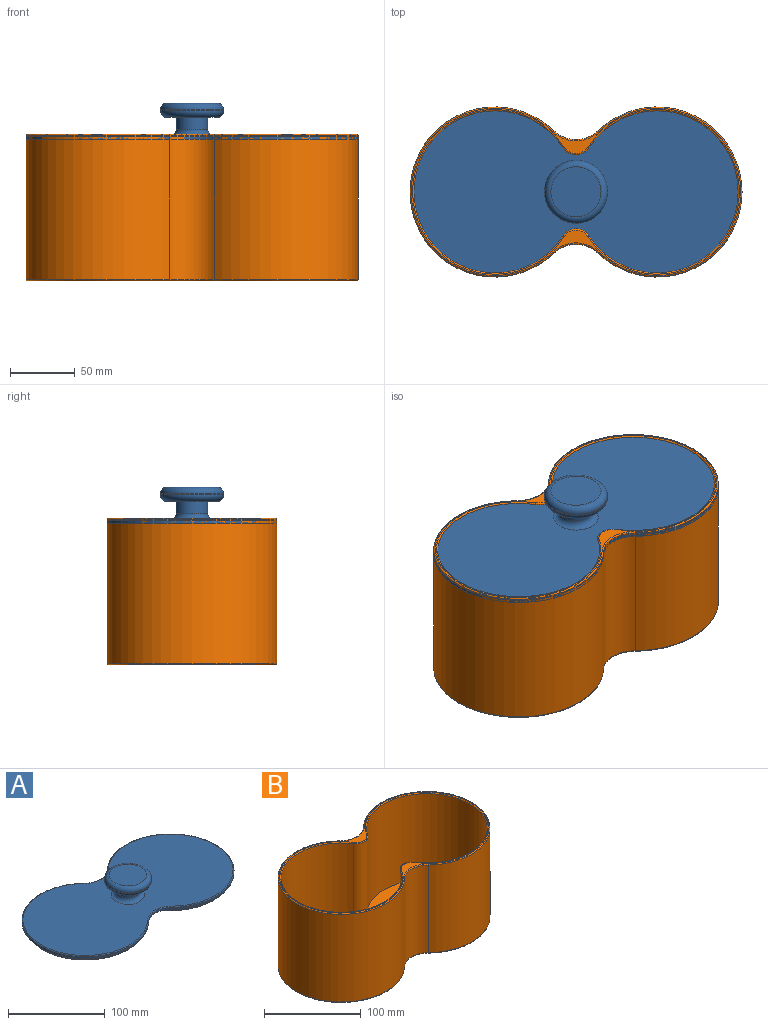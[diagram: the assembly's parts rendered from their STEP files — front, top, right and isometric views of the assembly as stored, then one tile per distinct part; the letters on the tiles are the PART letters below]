
ASSEMBLY  parts=2 mates=1
PART A: 26 faces, bbox 266.8x141.8x33 mm
  f0: cylinder r=24.76mm len=34.29mm, axis (0,0,-1), area 75.8mm2, adj f1,f3,f5,f22
  f1: cylinder r=65.5mm len=131mm, axis (0,0,-1), area 611.9mm2, adj f0,f2,f5,f23
  f2: cylinder r=24.76mm len=34.29mm, axis (0,0,-1), area 75.8mm2, adj f1,f3,f5,f25
  f3: cylinder r=65.5mm len=131mm, axis (0,0,-1), area 611.9mm2, adj f0,f2,f5,f24
  f4: plane 254x129mm, normal (0,0,1), area 25634.6mm2, adj f15,f22,f23,f24,f25
  f5: plane 256x131mm, normal (0,0,-1), area 2760.7mm2, adj f0,f1,f2,f3,f6,f7,f8,f9
  f6: cylinder r=12.4mm len=20.83mm, axis (0,0,1), area 98.9mm2, adj f5,f7,f9,f18
  f7: cylinder r=62mm len=124mm, axis (0,0,1), area 1273.8mm2, adj f5,f6,f8,f20
  f8: cylinder r=12.4mm len=20.83mm, axis (0,0,1), area 98.9mm2, adj f5,f7,f9,f21
  f9: cylinder r=62mm len=124mm, axis (0,0,1), area 1273.8mm2, adj f5,f6,f8,f19
  f10: plane 247x122mm, normal (0,0,-1), area 23799.4mm2, adj f18,f19,f20,f21
  f11: cylinder r=12.15mm len=24.3mm, axis (0,0,-1), area 687.2mm2, adj f12,f15
  f12: plane 38.63x38.63mm, normal (0,0,-1), area 708.3mm2, adj f11,f16
  f13: plane 38.63x38.63mm, normal (0,0,1), area 1172.2mm2, adj f17
  f14: cylinder r=24.32mm len=48.63mm, axis (0,0,-1), area 152.8mm2, adj f16,f17
  f15: torus R=17.15mm, axis (0,0,1), area 689.3mm2, adj f4,f11
  f16: torus R=19.32mm, axis (0,0,1), area 1110.3mm2, adj f12,f14
  f17: torus R=19.32mm, axis (0,0,1), area 1110.3mm2, adj f13,f14
  f18: torus R=13.4mm, axis (0,0,1), area 40mm2, adj f6,f10,f19,f20
  f19: torus R=61mm, axis (0,0,1), area 497.3mm2, adj f9,f10,f18,f21
  f20: torus R=61mm, axis (0,0,1), area 497.3mm2, adj f7,f10,f18,f21
  f21: torus R=13.4mm, axis (0,0,1), area 40mm2, adj f8,f10,f19,f20
  f22: torus R=25.76mm, axis (0,0,1), area 60.4mm2, adj f0,f4,f23,f24
  f23: torus R=64.5mm, axis (0,0,1), area 478mm2, adj f1,f4,f22,f25
  f24: torus R=64.5mm, axis (0,0,1), area 478mm2, adj f3,f4,f22,f25
  f25: torus R=25.76mm, axis (0,0,1), area 60.4mm2, adj f2,f4,f23,f24
PART B: 23 faces, bbox 266.8x141.8x113 mm
  f0: cylinder r=24.76mm len=111mm, axis (0,0,-1), area 4204.2mm2, adj f1,f3,f18,f20
  f1: cylinder r=65.5mm len=131mm, axis (0,0,-1), area 33963mm2, adj f0,f2,f16,f22
  f2: cylinder r=24.76mm len=111mm, axis (0,0,-1), area 4204.2mm2, adj f1,f3,f15,f21
  f3: cylinder r=65.5mm len=131mm, axis (0,0,-1), area 33963mm2, adj f0,f2,f17,f19
  f4: plane 254x129mm, normal (0,0,-1), area 26558.8mm2, adj f19,f20,f21,f22
  f5: cylinder r=62.5mm len=125mm, axis (0,0,-1), area 34991.8mm2, adj f6,f8,f10,f12
  f6: cylinder r=11.9mm len=109mm, axis (0,0,-1), area 2587.2mm2, adj f5,f7,f10,f11
  f7: cylinder r=62.5mm len=125mm, axis (0,0,-1), area 34991.8mm2, adj f6,f8,f10,f13
  f8: cylinder r=11.9mm len=109mm, axis (0,0,-1), area 2587.2mm2, adj f5,f7,f10,f14
  f9: plane 254x129mm, normal (0,0,1), area 1039.5mm2, adj f11,f12,f13,f14,f15,f16,f17,f18
  f10: plane 250x125mm, normal (0,0,1), area 24826.7mm2, adj f5,f6,f7,f8
  f11: torus R=10.9mm, axis (0,0,1), area 36.1mm2, adj f6,f9,f12,f13
  f12: torus R=63.5mm, axis (0,0,1), area 507.2mm2, adj f5,f9,f11,f14
  f13: torus R=63.5mm, axis (0,0,1), area 507.2mm2, adj f7,f9,f11,f14
  f14: torus R=10.9mm, axis (0,0,1), area 36.1mm2, adj f8,f9,f12,f13
  f15: torus R=25.76mm, axis (0,0,1), area 60.4mm2, adj f2,f9,f16,f17
  f16: torus R=64.5mm, axis (0,0,1), area 478mm2, adj f1,f9,f15,f18
  f17: torus R=64.5mm, axis (0,0,1), area 478mm2, adj f3,f9,f15,f18
  f18: torus R=25.76mm, axis (0,0,1), area 60.4mm2, adj f0,f9,f16,f17
  f19: torus R=64.5mm, axis (0,0,1), area 478mm2, adj f3,f4,f20,f21
  f20: torus R=25.76mm, axis (0,0,1), area 60.4mm2, adj f0,f4,f19,f22
  f21: torus R=25.76mm, axis (0,0,1), area 60.4mm2, adj f2,f4,f19,f22
  f22: torus R=64.5mm, axis (0,0,1), area 478mm2, adj f1,f4,f20,f21
PLACE A t=(-0.69,149.93,195.52)mm
PLACE B t=(-0.69,149.93,86.52)mm
MATE slider A.f1 <-> B.f7  axis (0,0,1) through (-63.19,149.93,198.52)mm
